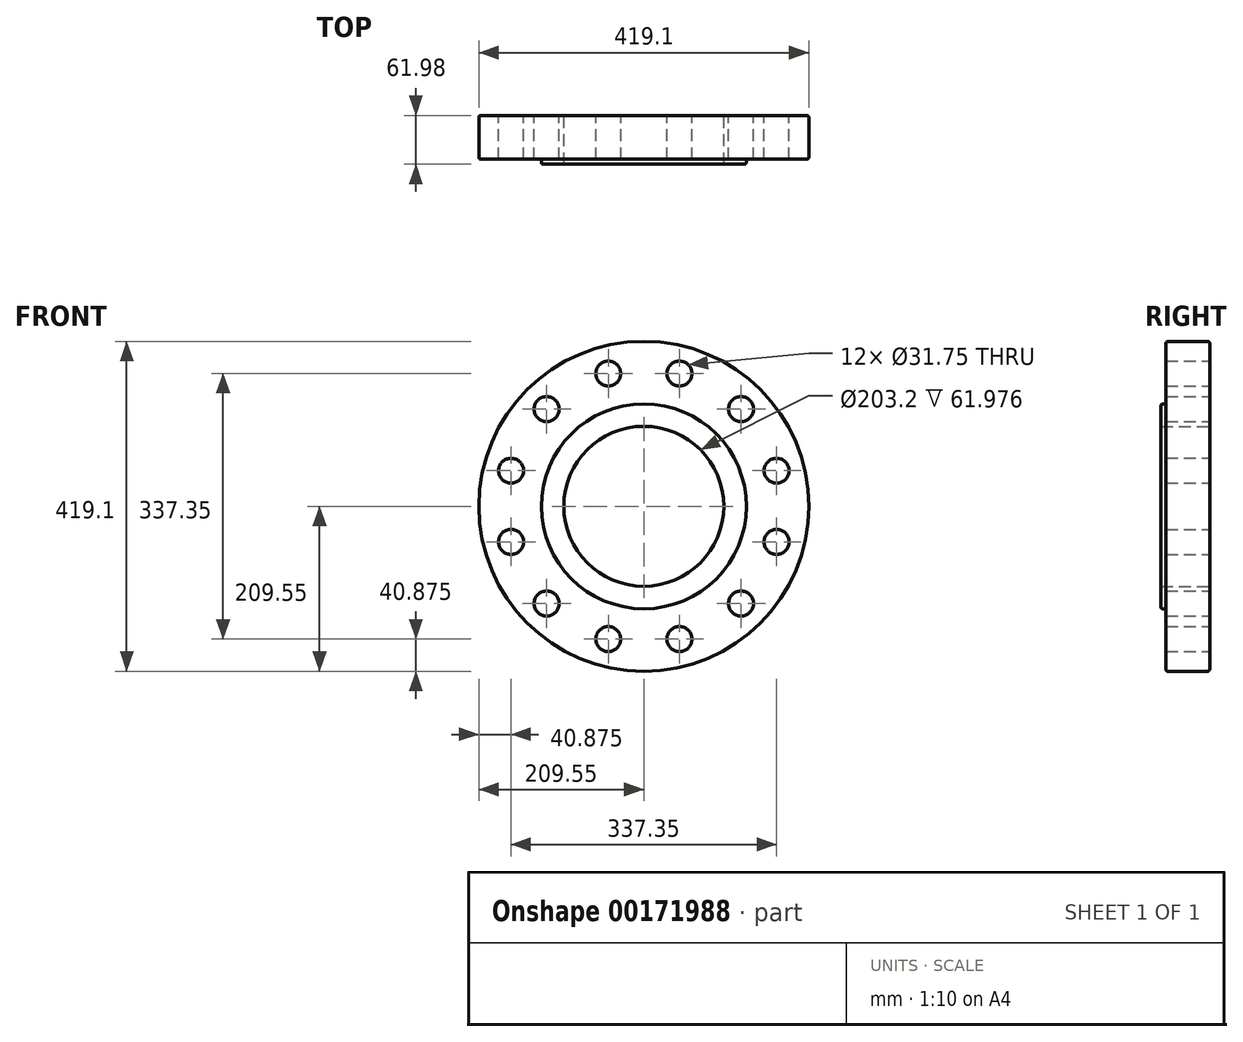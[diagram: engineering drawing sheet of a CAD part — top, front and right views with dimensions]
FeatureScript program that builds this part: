
annotation { "Feature Type Name" : "Feature", "Feature Type Description" : "" }
export const myFeature = defineFeature(function(context is Context, id is Id, definition is map)
    precondition{}
    {
        {
            var Q0;
            Q0=qCreatedBy(makeId("Front.planeOp"),FACE);
            var sketch = newSketch(context, id + "F0", { "sketchPlane" : qUnion([Q0])});
            skCircle(sketch, "E0", {"center": v(0, 0) * mm, "radius": 209.55 * mm});
            skCircle(sketch, "E1", {"center": v(0, 0) * mm, "radius": 101.6 * mm});
            skCircle(sketch, "E2", {"center": v(45.2, 168.67) * mm, "radius": 15.88 * mm});
            skCircle(sketch, "E3.1.0", {"center": v(-45.2, 168.67) * mm, "radius": 15.88 * mm});
            skCircle(sketch, "E3.2.0", {"center": v(-123.48, 123.48) * mm, "radius": 15.88 * mm});
            skCircle(sketch, "E3.3.0", {"center": v(-168.67, 45.2) * mm, "radius": 15.88 * mm});
            skCircle(sketch, "E3.4.0", {"center": v(-168.67, -45.2) * mm, "radius": 15.88 * mm});
            skCircle(sketch, "E3.5.0", {"center": v(-123.48, -123.48) * mm, "radius": 15.88 * mm});
            skCircle(sketch, "E3.6.0", {"center": v(-45.2, -168.67) * mm, "radius": 15.88 * mm});
            skCircle(sketch, "E3.7.0", {"center": v(45.2, -168.67) * mm, "radius": 15.88 * mm});
            skCircle(sketch, "E3.8.0", {"center": v(123.48, -123.48) * mm, "radius": 15.88 * mm});
            skCircle(sketch, "E3.9.0", {"center": v(168.67, -45.2) * mm, "radius": 15.88 * mm});
            skCircle(sketch, "E3.10.0", {"center": v(168.67, 45.2) * mm, "radius": 15.88 * mm});
            skCircle(sketch, "E3.11.0", {"center": v(123.48, 123.48) * mm, "radius": 15.88 * mm});
            skSolve(sketch);
        }
        {
            var Q0;
            Q0=qSketchRegion(id+"F0",true);
            extrude(context, id + "F1", {"entities" : qUnion([Q0]), "depth" : 55.63 * mm});
        }
        {
            var Q0;
            Q0=makeQuery(id+"F1.opExtrude","CAP_FACE",FACE,{"disambiguationData":[OSD([sQuery(id+"F0.wireOp",EDGE,"E0"),sQuery(id+"F0.wireOp",EDGE,"E1"),sQuery(id+"F0.wireOp",EDGE,"E2"),sQuery(id+"F0.wireOp",EDGE,"E3.1.0"),sQuery(id+"F0.wireOp",EDGE,"E3.2.0"),sQuery(id+"F0.wireOp",EDGE,"E3.3.0"),sQuery(id+"F0.wireOp",EDGE,"E3.4.0"),sQuery(id+"F0.wireOp",EDGE,"E3.5.0"),sQuery(id+"F0.wireOp",EDGE,"E3.6.0"),sQuery(id+"F0.wireOp",EDGE,"E3.7.0"),sQuery(id+"F0.wireOp",EDGE,"E3.8.0"),sQuery(id+"F0.wireOp",EDGE,"E3.9.0"),sQuery(id+"F0.wireOp",EDGE,"E3.10.0"),sQuery(id+"F0.wireOp",EDGE,"E3.11.0")])],"isStart":false});
            var sketch = newSketch(context, id + "F2", { "sketchPlane" : qUnion([Q0])});
            skCircle(sketch, "E4", {"center": v(0, 0) * mm, "radius": 130.18 * mm});
            skCircle(sketch, "E5", {"center": v(0, 0) * mm, "radius": 101.6 * mm});
            skSolve(sketch);
        }
        {
            var Q0;
            Q0=qSketchRegion(id+"F2",true);
            extrude(context, id + "F3", {"entities" : qUnion([Q0]), "operationType" : NewBodyOperationType.ADD, "depth" : 6.35 * mm});
        }
        {
            var Q0;
            Q0=makeQuery(id+"F1.opExtrude","CAP_EDGE",EDGE,{"disambiguationData":[OSD([sQuery(id+"F0.wireOp",EDGE,"E0")])],"isStart":false});
            var Q1;
            Q1=makeQuery(id+"F1.opExtrude","CAP_EDGE",EDGE,{"disambiguationData":[OSD([sQuery(id+"F0.wireOp",EDGE,"E0")])],"isStart":true});
            var Q2;
            Q2=makeQuery(id+"F3.opExtrude","CAP_EDGE",EDGE,{"disambiguationData":[OSD([sQuery(id+"F2.wireOp",EDGE,"E4")])],"isStart":false});
            var Q3;
            Q3=makeQuery(id+"F3.opExtrude","CAP_EDGE",EDGE,{"disambiguationData":[OSD([sQuery(id+"F2.wireOp",EDGE,"E4")])],"isStart":true});
            fillet(context, id + "F4", {"entities" : qUnion([Q0, Q1, Q2, Q3]), "radius" : 2.54 * mm, "tangentPropagation" : true, "allowEdgeOverflow" : false});
        }
    });
